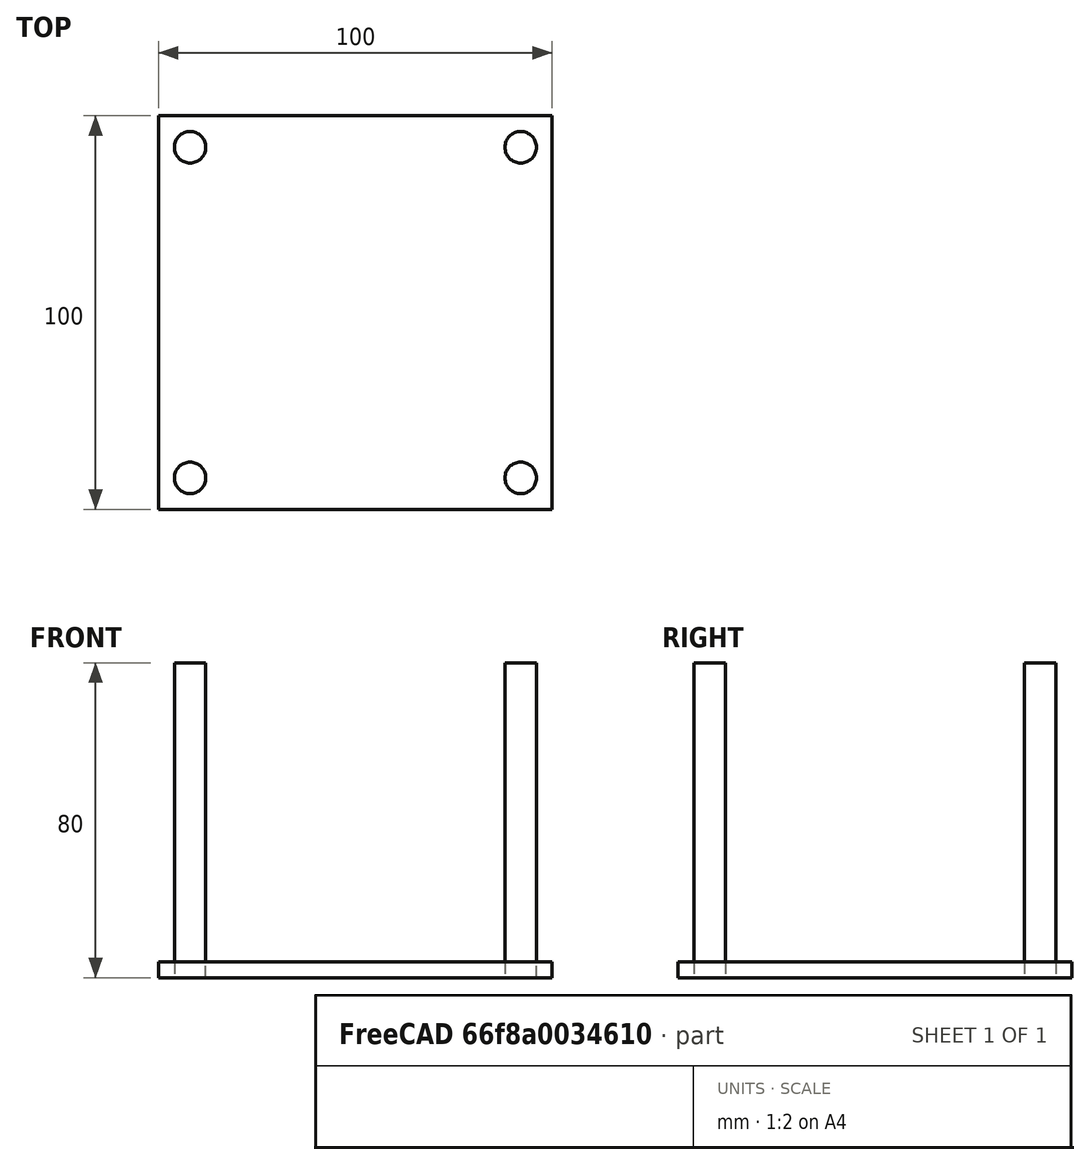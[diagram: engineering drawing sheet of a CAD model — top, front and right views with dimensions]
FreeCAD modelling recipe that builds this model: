
FCSTD DOCUMENT  (FreeCAD 0.21R33668 +26 (Git))
Label: table
License: All rights reserved
LicenseURL: http://en.wikipedia.org/wiki/All_rights_reserved
objects: Part::Cylinder×4, Part::Box×1
note: 5 computed .brp shape members not serialized (recipe doc carries the construction recipe); baked Part::Feature solids carry a one-line shape summary decoded from their .brp

FEATURE [Part::Box] Box  label="Cube"
  AttacherType = Attacher::AttachEngine3D
  Height = 4
  Length = 100
  Placement = pos=(0,0,80) rot=(0,0,1;0rad)
  Width = 100
  expr: .Placement.Base.z = 80 mm
FEATURE [Part::Cylinder] Cylinder  label="Cylindre"
  Angle = 360
  AttacherType = Attacher::AttachEngine3D
  FirstAngle = 0
  Height = 80
  Placement = pos=(8,8,80) rot=(0,0,1;0rad)
  Radius = 4
  SecondAngle = 0
  expr: .Placement.Base.y = 8 mm
FEATURE [Part::Cylinder] Cylinder001  label="Cylindre001"
  Angle = 360
  AttacherType = Attacher::AttachEngine3D
  FirstAngle = 0
  Height = 80
  Placement = pos=(92,8,80) rot=(0,0,1;0rad)
  Radius = 4
  SecondAngle = 0
  expr: .Placement.Base.y = 8 mm
FEATURE [Part::Cylinder] Cylinder002  label="Cylindre002"
  Angle = 360
  AttacherType = Attacher::AttachEngine3D
  FirstAngle = 0
  Height = 80
  Placement = pos=(92,92,80) rot=(0,0,1;0rad)
  Radius = 4
  SecondAngle = 0
  expr: .Placement.Base.y = 92 mm
FEATURE [Part::Cylinder] Cylinder003  label="Cylindre003"
  Angle = 360
  AttacherType = Attacher::AttachEngine3D
  FirstAngle = 0
  Height = 80
  Placement = pos=(8,92,80) rot=(0,0,1;0rad)
  Radius = 4
  SecondAngle = 0
  expr: .Placement.Base.x = 8 mm
  expr: .Placement.Base.y = 92 mm
